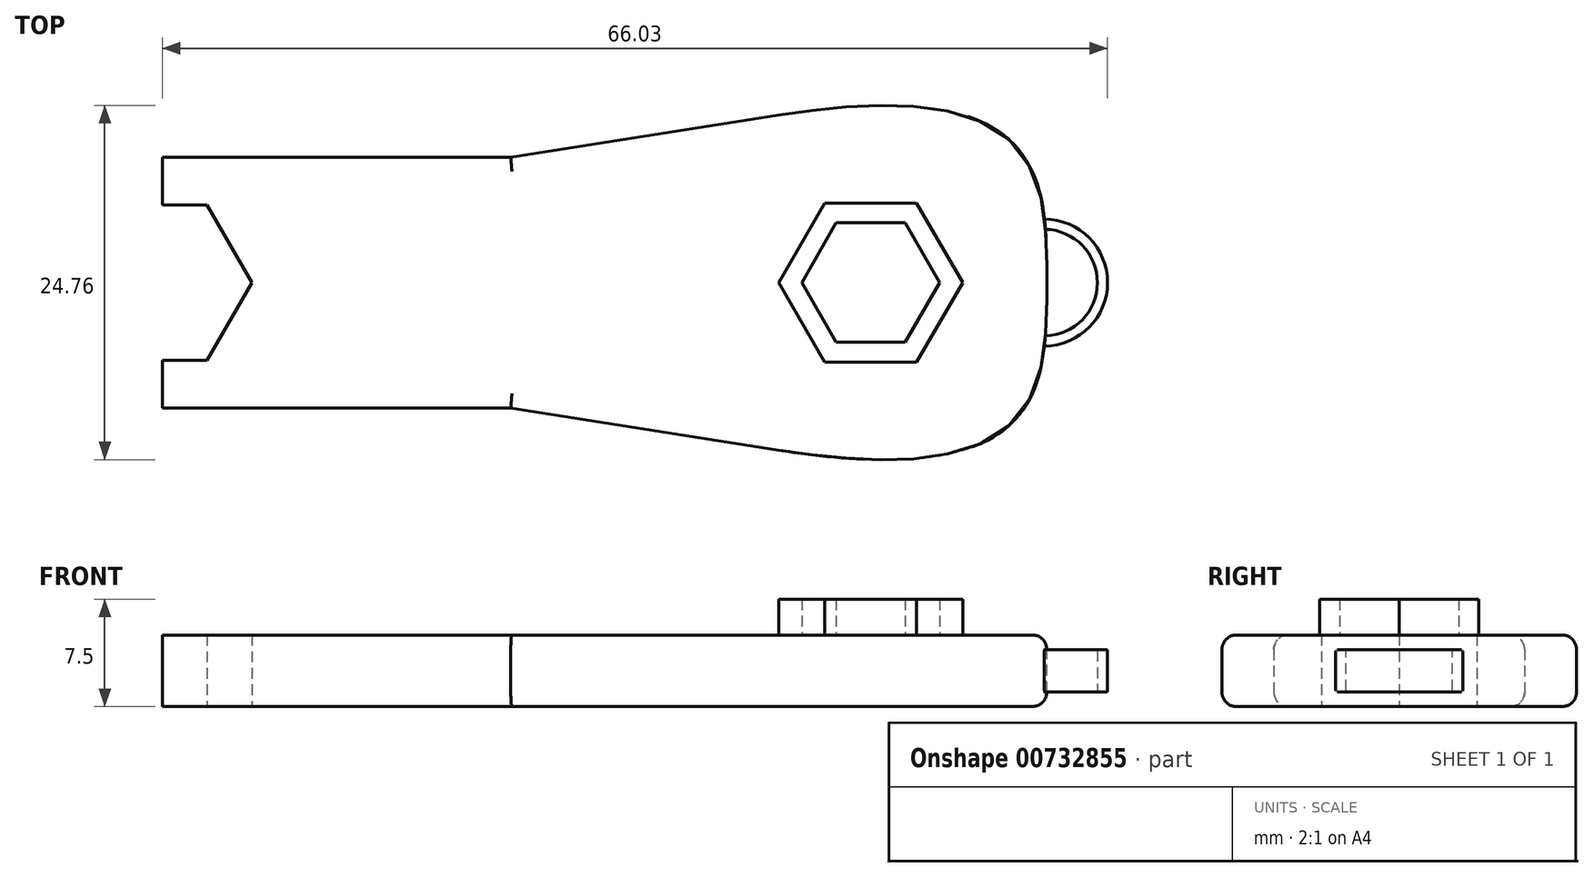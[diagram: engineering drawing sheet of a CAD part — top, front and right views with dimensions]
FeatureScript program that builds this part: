
annotation { "Feature Type Name" : "Feature", "Feature Type Description" : "" }
export const myFeature = defineFeature(function(context is Context, id is Id, definition is map)
    precondition{}
    {
        {
            var Q0;
            Q0=qCreatedBy(makeId("Top.planeOp"),FACE);
            var sketch = newSketch(context, id + "F0", { "sketchPlane" : qUnion([Q0])});
            skLineSegment(sketch, "E0.bottom", {"start": v(18.72, 14.66) * mm, "end": v(-18.72, 14.66) * mm});
            skLineSegment(sketch, "E0.top", {"start": v(18.72, -14.66) * mm, "end": v(-18.72, -14.66) * mm});
            skLineSegment(sketch, "E0.left", {"start": v(18.72, 14.66) * mm, "end": v(18.72, -14.66) * mm});
            skLineSegment(sketch, "E0.right", {"start": v(-18.72, 14.66) * mm, "end": v(-18.72, -14.66) * mm});
            skLineSegment(sketch, "E1", {"start": v(-18.72, 8.76) * mm, "end": v(-43.07, 8.76) * mm});
            skLineSegment(sketch, "E2", {"start": v(-43.07, 8.76) * mm, "end": v(-43.07, 0) * mm});
            skLineSegment(sketch, "E3", {"start": v(-43.07, 0) * mm, "end": v(-18.72, 0) * mm});
            skLineSegment(sketch, "E4.MirrorCS", {"start": v(-43.07, -8.76) * mm, "end": v(-43.07, 0) * mm});
            skLineSegment(sketch, "E5.MirrorCS", {"start": v(-18.72, -8.76) * mm, "end": v(-43.07, -8.76) * mm});
            skLineSegment(sketch, "E6", {"start": v(-18.72, -8.76) * mm, "end": v(18.72, -14.66) * mm});
            skLineSegment(sketch, "E7", {"start": v(-18.72, 8.76) * mm, "end": v(18.72, 14.66) * mm});
            skCircle(sketch, "E8.cCircle", {"center": v(-43.07, 0) * mm, "radius": 6.27 * mm, "construction": true});
            skLineSegment(sketch, "E8.0", {"start": v(-36.8, 0) * mm, "end": v(-39.93, -5.43) * mm});
            skLineSegment(sketch, "E8.1", {"start": v(-39.93, -5.43) * mm, "end": v(-46.2, -5.43) * mm});
            skLineSegment(sketch, "E8.2", {"start": v(-46.2, -5.43) * mm, "end": v(-49.34, 0) * mm});
            skLineSegment(sketch, "E8.3", {"start": v(-49.34, 0) * mm, "end": v(-46.2, 5.43) * mm});
            skLineSegment(sketch, "E8.4", {"start": v(-46.2, 5.43) * mm, "end": v(-39.93, 5.43) * mm});
            skLineSegment(sketch, "E8.5", {"start": v(-39.93, 5.43) * mm, "end": v(-36.8, 0) * mm});
            skSolve(sketch);
        }
        {
            var Q0;
            {var subQ6=sQuery(id+"F0.wireOp",EDGE,"E1");Q0=makeQuery(id+"F0.imprint","IMPRINT",FACE,{"disambiguationData":[TD([[makeQuery(id+"F0.imprint","IMPRINT",EDGE,{"derivedFrom":subQ6}),1.0]])]});}
            var Q1;
            {var subQ0=sQuery(id+"F0.wireOp",EDGE,"E5.MirrorCS");Q1=makeQuery(id+"F0.imprint","IMPRINT",FACE,{"disambiguationData":[TD([[makeQuery(id+"F0.imprint","IMPRINT",EDGE,{"derivedFrom":subQ0}),-1.0]])]});}
            var Q2;
            Q2=makeQuery(id+"F0.imprint","IMPRINT",FACE,{"disambiguationData":[TD([[makeQuery(id+"F0.imprint","IMPRINT",EDGE,{"derivedFrom":sQuery(id+"F0.wireOp",EDGE,"E0.left")}),-1.0]])]});
            var Q3;
            Q3=makeQuery(id+"F0.imprint","IMPRINT",FACE,{"disambiguationData":[TD([[makeQuery(id+"F0.imprint","IMPRINT",EDGE,{"derivedFrom":sQuery(id+"F0.wireOp",EDGE,"91cd465d-1edd-453e-acd5-d07138ded2c4.0")}),-1.0]])]});
            var Q4;
            Q4=makeQuery(id+"F0.imprint","IMPRINT",FACE,{"disambiguationData":[TD([[makeQuery(id+"F0.imprint","IMPRINT",EDGE,{"derivedFrom":sQuery(id+"F0.wireOp",EDGE,"c5f50209-c7f5-4414-94c8-9683472f1612.0")}),-1.0]])]});
            extrude(context, id + "F1", {"entities" : qUnion([Q0, Q1, Q2, Q3, Q4]), "depth" : 5 * mm, "offsetDistance" : 25 * mm});
        }
        {
            var Q0;
            Q0=makeQuery(id+"F1.opExtrude","CAP_FACE",FACE,{"disambiguationData":[OSD([sQuery(id+"F0.wireOp",EDGE,"E0.left"),sQuery(id+"F0.wireOp",EDGE,"E1"),sQuery(id+"F0.wireOp",EDGE,"E2"),sQuery(id+"F0.wireOp",EDGE,"E4.MirrorCS"),sQuery(id+"F0.wireOp",EDGE,"E5.MirrorCS"),sQuery(id+"F0.wireOp",EDGE,"E6"),sQuery(id+"F0.wireOp",EDGE,"E7"),sQuery(id+"F0.wireOp",EDGE,"1878632b-6eda-4864-b583-b625bd42ca04.0"),sQuery(id+"F0.wireOp",EDGE,"1878632b-6eda-4864-b583-b625bd42ca04.1"),sQuery(id+"F0.wireOp",EDGE,"1878632b-6eda-4864-b583-b625bd42ca04.2"),sQuery(id+"F0.wireOp",EDGE,"1878632b-6eda-4864-b583-b625bd42ca04.8"),sQuery(id+"F0.wireOp",EDGE,"1878632b-6eda-4864-b583-b625bd42ca04.9")])],"isStart":false});
            var sketch = newSketch(context, id + "F2", { "sketchPlane" : qUnion([Q0])});
            skFitSpline(sketch, "E9", {"points": [v(0, 11.71) * mm, v(18.72, 0) * mm, v(0, -11.71) * mm], "startDerivative": vector(112.32, 17.7) * mm, "endDerivative": vector(-112.32, 17.7) * mm});
            skLineSegment(sketch, "E10", {"start": v(0, 11.71) * mm, "end": v(0, -11.71) * mm});
            skSolve(sketch);
        }
        {
            var Q0;
            {var subQ1=makeQuery(id+"F1.opExtrude","CAP_EDGE",EDGE,{"disambiguationData":[OSD([sQuery(id+"F0.wireOp",EDGE,"E6")])],"isStart":false});var subQ3=makeQuery(id+"F1.opExtrude","CAP_EDGE",EDGE,{"disambiguationData":[OSD([sQuery(id+"F0.wireOp",EDGE,"E0.left")])],"isStart":false});var subQ5=makeQuery(id+"F2.imprint","INTERSECT",VERTEX,{"derivedFrom":[subQ3,subQ1]});Q0=makeQuery(id+"F2.imprint","IMPRINT",FACE,{"disambiguationData":[TD([[makeQuery(id+"F2.imprint","IMPRINT",EDGE,{"disambiguationData":[TD([[subQ5,1.0]])],"derivedFrom":subQ3}),-1.0]])]});}
            var Q1;
            {var subQ1=makeQuery(id+"F1.opExtrude","CAP_EDGE",EDGE,{"disambiguationData":[OSD([sQuery(id+"F0.wireOp",EDGE,"E7")])],"isStart":false});var subQ3=makeQuery(id+"F1.opExtrude","CAP_EDGE",EDGE,{"disambiguationData":[OSD([sQuery(id+"F0.wireOp",EDGE,"E0.left")])],"isStart":false});var subQ5=makeQuery(id+"F2.imprint","INTERSECT",VERTEX,{"derivedFrom":[subQ3,subQ1]});Q1=makeQuery(id+"F2.imprint","IMPRINT",FACE,{"disambiguationData":[TD([[makeQuery(id+"F2.imprint","IMPRINT",EDGE,{"disambiguationData":[TD([[subQ5,-1.0]])],"derivedFrom":subQ3}),-1.0]])]});}
            extrude(context, id + "F3", {"entities" : qUnion([Q0, Q1]), "operationType" : NewBodyOperationType.REMOVE, "oppositeDirection" : true, "depth" : 25 * mm, "offsetDistance" : 25 * mm});
        }
        {
            var Q0;
            Q0=makeQuery(id+"F1.opExtrude","CAP_EDGE",EDGE,{"disambiguationData":[OSD([sQuery(id+"F0.wireOp",EDGE,"E5.MirrorCS")])],"isStart":false});
            var Q1;
            Q1=makeQuery(id+"F1.opExtrude","CAP_EDGE",EDGE,{"disambiguationData":[OSD([sQuery(id+"F0.wireOp",EDGE,"E6")])],"isStart":false});
            var Q2;
            Q2=makeQuery(id+"F1.opExtrude","CAP_EDGE",EDGE,{"disambiguationData":[OSD([sQuery(id+"F0.wireOp",EDGE,"E1")])],"isStart":false});
            var Q3;
            Q3=makeQuery(id+"F1.opExtrude","CAP_EDGE",EDGE,{"disambiguationData":[OSD([sQuery(id+"F0.wireOp",EDGE,"E5.MirrorCS")])],"isStart":true});
            var Q4;
            Q4=makeQuery(id+"F1.opExtrude","CAP_EDGE",EDGE,{"disambiguationData":[OSD([sQuery(id+"F0.wireOp",EDGE,"E6")])],"isStart":true});
            var Q5;
            Q5=makeQuery(id+"F1.opExtrude","CAP_EDGE",EDGE,{"disambiguationData":[OSD([sQuery(id+"F0.wireOp",EDGE,"E1")])],"isStart":true});
            fillet(context, id + "F4", {"entities" : qUnion([Q0, Q1, Q2, Q3, Q4, Q5]), "radius" : 1 * mm, "tangentPropagation" : true, "allowEdgeOverflow" : false});
        }
        {
            var Q0;
            Q0=makeQuery(id+"F1.opExtrude","SWEPT_FACE",FACE,{"disambiguationData":[OSD([sQuery(id+"F0.wireOp",EDGE,"E4.MirrorCS")])]});
            cPlane(context, id + "F5", {"entities" : qUnion([Q0]), "cplaneType" : CPlaneType.OFFSET, "offset" : 61.6 * mm, "oppositeDirection" : true, "width" : 150 * mm, "height" : 150 * mm});
        }
        {
            var Q0;
            Q0=qCreatedBy(id+"F5.planeOp",FACE);
            var sketch = newSketch(context, id + "F6", { "sketchPlane" : qUnion([Q0])});
            skLineSegment(sketch, "E11", {"start": v(4.43, 3.99) * mm, "end": v(4.43, 1.01) * mm});
            skLineSegment(sketch, "E12", {"start": v(3.73, 3.99) * mm, "end": v(3.73, 1.03) * mm});
            skLineSegment(sketch, "E13", {"start": v(3.73, 3.99) * mm, "end": v(4.43, 3.99) * mm});
            skLineSegment(sketch, "E14", {"start": v(4.43, 1.01) * mm, "end": v(3.73, 1.03) * mm});
            skLineSegment(sketch, "E15", {"start": v(0, 1) * mm, "end": v(0, 4) * mm});
            skSolve(sketch);
        }
        {
            var Q0;
            Q0 = qSketchRegion(id + "F6", true);
            var Q1;
            Q1=sQuery(id+"F6.wireOp",EDGE,"E15");
            revolve(context, id + "F7", {"operationType" : NewBodyOperationType.ADD, "surfaceOperationType" : NewSurfaceOperationType.NEW, "entities" : qUnion([Q0]), "axis" : qUnion([Q1]), "revolveType" : RevolveType.FULL});
        }
        {
            var Q0;
            Q0=makeQuery(id+"F7.opRevolve","SWEPT_EDGE",EDGE,{"disambiguationData":[OSD([sQuery(id+"F6.wireOp",EDGE,"E11"),sQuery(id+"F6.wireOp",EDGE,"E13")])]});
            var Q1;
            Q1=makeQuery(id+"F7.opRevolve","SWEPT_EDGE",EDGE,{"disambiguationData":[OSD([sQuery(id+"F6.wireOp",EDGE,"E12"),sQuery(id+"F6.wireOp",EDGE,"E13")])]});
            var Q2;
            Q2=makeQuery(id+"F7.opRevolve","SWEPT_EDGE",EDGE,{"disambiguationData":[OSD([sQuery(id+"F6.wireOp",EDGE,"E12"),sQuery(id+"F6.wireOp",EDGE,"E14")])]});
            var Q3;
            Q3=makeQuery(id+"F7.opRevolve","SWEPT_EDGE",EDGE,{"disambiguationData":[OSD([sQuery(id+"F6.wireOp",EDGE,"E11"),sQuery(id+"F6.wireOp",EDGE,"E14")])]});
            fillet(context, id + "F8", {"entities" : qUnion([Q0, Q1, Q2, Q3]), "radius" : 0.1 * mm, "tangentPropagation" : true, "allowEdgeOverflow" : false});
        }
        {
            var Q0;
            Q0=makeQuery(id+"F1.opExtrude","CAP_FACE",FACE,{"disambiguationData":[OSD([sQuery(id+"F0.wireOp",EDGE,"E0.left"),sQuery(id+"F0.wireOp",EDGE,"E1"),sQuery(id+"F0.wireOp",EDGE,"E2"),sQuery(id+"F0.wireOp",EDGE,"E4.MirrorCS"),sQuery(id+"F0.wireOp",EDGE,"E5.MirrorCS"),sQuery(id+"F0.wireOp",EDGE,"E6"),sQuery(id+"F0.wireOp",EDGE,"E7"),sQuery(id+"F0.wireOp",EDGE,"1878632b-6eda-4864-b583-b625bd42ca04.0"),sQuery(id+"F0.wireOp",EDGE,"1878632b-6eda-4864-b583-b625bd42ca04.1"),sQuery(id+"F0.wireOp",EDGE,"1878632b-6eda-4864-b583-b625bd42ca04.2"),sQuery(id+"F0.wireOp",EDGE,"1878632b-6eda-4864-b583-b625bd42ca04.8"),sQuery(id+"F0.wireOp",EDGE,"1878632b-6eda-4864-b583-b625bd42ca04.9")])],"isStart":false});
            var sketch = newSketch(context, id + "F9", { "sketchPlane" : qUnion([Q0])});
            skCircle(sketch, "E16.cCircle", {"center": v(6.42, 0) * mm, "radius": 6.42 * mm, "construction": true});
            skLineSegment(sketch, "E16.0", {"start": v(0, 0) * mm, "end": v(3.21, 5.56) * mm});
            skLineSegment(sketch, "E16.1", {"start": v(3.21, 5.56) * mm, "end": v(9.63, 5.56) * mm});
            skLineSegment(sketch, "E16.2", {"start": v(9.63, 5.56) * mm, "end": v(12.84, 0) * mm});
            skLineSegment(sketch, "E16.3", {"start": v(12.84, 0) * mm, "end": v(9.63, -5.56) * mm});
            skLineSegment(sketch, "E16.4", {"start": v(9.63, -5.56) * mm, "end": v(3.21, -5.56) * mm});
            skLineSegment(sketch, "E16.5", {"start": v(3.21, -5.56) * mm, "end": v(0, 0) * mm});
            skCircle(sketch, "E17.cCircle", {"center": v(6.42, 0) * mm, "radius": 4.82 * mm, "construction": true});
            skPoint(sketch, "E17.cCircle.perimeterSnap0", {"position": v(1.6, 2.78) * mm});
            skLineSegment(sketch, "E17.0", {"start": v(1.6, 0) * mm, "end": v(4.01, 4.17) * mm});
            skPoint(sketch, "E17.0.startSnap0", {"position": v(1.6, 2.78) * mm});
            skLineSegment(sketch, "E17.1", {"start": v(4.01, 4.17) * mm, "end": v(8.83, 4.17) * mm});
            skLineSegment(sketch, "E17.2", {"start": v(8.83, 4.17) * mm, "end": v(11.24, 0) * mm});
            skLineSegment(sketch, "E17.3", {"start": v(11.24, 0) * mm, "end": v(8.83, -4.17) * mm});
            skLineSegment(sketch, "E17.4", {"start": v(8.83, -4.17) * mm, "end": v(4.01, -4.17) * mm});
            skLineSegment(sketch, "E17.5", {"start": v(4.01, -4.17) * mm, "end": v(1.6, 0) * mm});
            skSolve(sketch);
        }
        {
            var Q0;
            Q0 = qSketchRegion(id + "F9", true);
            extrude(context, id + "F10", {"entities" : qUnion([Q0]), "operationType" : NewBodyOperationType.ADD, "depth" : 2.5 * mm, "offsetDistance" : 25 * mm});
        }
    });
